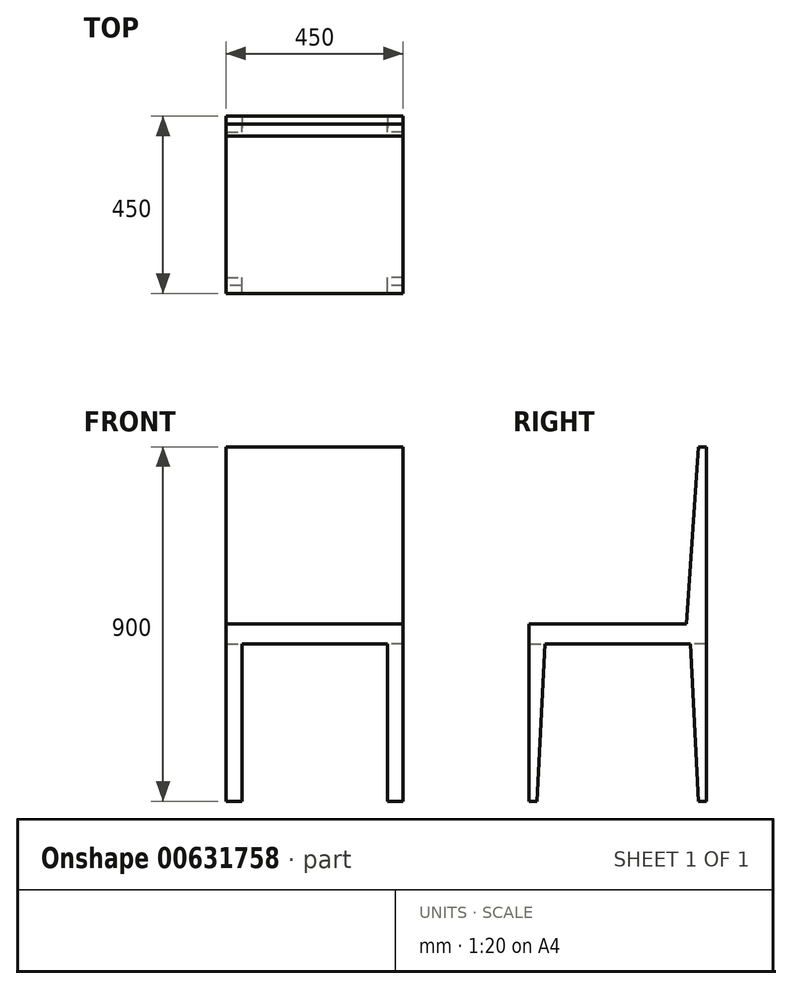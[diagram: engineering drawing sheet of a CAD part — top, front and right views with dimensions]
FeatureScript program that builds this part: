
annotation { "Feature Type Name" : "Feature", "Feature Type Description" : "" }
export const myFeature = defineFeature(function(context is Context, id is Id, definition is map)
    precondition{}
    {
        {
            var Q0;
            Q0=qCreatedBy(makeId("Top.planeOp"),FACE);
            var sketch = newSketch(context, id + "F0", { "sketchPlane" : qUnion([Q0])});
            skLineSegment(sketch, "E0.bottom", {"start": v(0, 0) * mm, "end": v(450, 0) * mm});
            skLineSegment(sketch, "E0.top", {"start": v(0, 450) * mm, "end": v(450, 450) * mm});
            skLineSegment(sketch, "E0.left", {"start": v(0, 0) * mm, "end": v(0, 450) * mm});
            skLineSegment(sketch, "E0.right", {"start": v(450, 0) * mm, "end": v(450, 450) * mm});
            skSolve(sketch);
        }
        {
            var Q0;
            Q0=makeQuery(id+"F0.imprint","IMPRINT",FACE,{"disambiguationData":[TD([[makeQuery(id+"F0.imprint","IMPRINT",EDGE,{"derivedFrom":sQuery(id+"F0.wireOp",EDGE,"E0.bottom")}),1.0]])]});
            extrude(context, id + "F1", {"entities" : qUnion([Q0]), "depth" : 50 * mm, "offsetDistance" : 25 * mm});
        }
        {
            var Q0;
            Q0=makeQuery(id+"F1.opExtrude","CAP_FACE",FACE,{"disambiguationData":[OSD([sQuery(id+"F0.wireOp",EDGE,"E0.bottom"),sQuery(id+"F0.wireOp",EDGE,"E0.top"),sQuery(id+"F0.wireOp",EDGE,"E0.left"),sQuery(id+"F0.wireOp",EDGE,"E0.right")])],"isStart":true});
            var sketch = newSketch(context, id + "F2", { "sketchPlane" : qUnion([Q0])});
            skLineSegment(sketch, "E1.bottom", {"start": v(0, -450) * mm, "end": v(40, -450) * mm});
            skLineSegment(sketch, "E1.top", {"start": v(0, -410) * mm, "end": v(40, -410) * mm});
            skLineSegment(sketch, "E1.left", {"start": v(0, -450) * mm, "end": v(0, -410) * mm});
            skLineSegment(sketch, "E1.right", {"start": v(40, -450) * mm, "end": v(40, -410) * mm});
            skSolve(sketch);
        }
        {
            var Q0;
            Q0=makeQuery(id+"F2.imprint","IMPRINT",FACE,{"disambiguationData":[TD([[makeQuery(id+"F2.imprint","IMPRINT",EDGE,{"derivedFrom":sQuery(id+"F2.wireOp",EDGE,"E1.bottom")}),1.0]])]});
            var Q1;
            Q1=sQuery(id+"F2.wireOp",EDGE,"E1.right");
            extrude(context, id + "F3", {"entities" : qUnion([Q0]), "operationType" : NewBodyOperationType.ADD, "surfaceEntities" : qUnion([Q1]), "depth" : 400 * mm, "offsetDistance" : 25 * mm});
        }
        {
            var Q0;
            Q0=makeQuery(id+"F1.opExtrude","CAP_FACE",FACE,{"disambiguationData":[OSD([sQuery(id+"F0.wireOp",EDGE,"E0.bottom"),sQuery(id+"F0.wireOp",EDGE,"E0.top"),sQuery(id+"F0.wireOp",EDGE,"E0.left"),sQuery(id+"F0.wireOp",EDGE,"E0.right")])],"isStart":true});
            var sketch = newSketch(context, id + "F4", { "sketchPlane" : qUnion([Q0])});
            skLineSegment(sketch, "E2.bottom", {"start": v(0, 0) * mm, "end": v(40, 0) * mm});
            skLineSegment(sketch, "E2.top", {"start": v(0, -40) * mm, "end": v(40, -40) * mm});
            skLineSegment(sketch, "E2.left", {"start": v(0, 0) * mm, "end": v(0, -40) * mm});
            skLineSegment(sketch, "E2.right", {"start": v(40, 0) * mm, "end": v(40, -40) * mm});
            skSolve(sketch);
        }
        {
            var Q0;
            Q0=makeQuery(id+"F4.imprint","IMPRINT",FACE,{"disambiguationData":[TD([[makeQuery(id+"F4.imprint","IMPRINT",EDGE,{"derivedFrom":sQuery(id+"F4.wireOp",EDGE,"E2.bottom")}),-1.0]])]});
            extrude(context, id + "F5", {"entities" : qUnion([Q0]), "operationType" : NewBodyOperationType.ADD, "depth" : 400 * mm, "offsetDistance" : 25 * mm});
        }
        {
            var Q0;
            Q0=makeQuery(id+"F1.opExtrude","CAP_FACE",FACE,{"disambiguationData":[OSD([sQuery(id+"F0.wireOp",EDGE,"E0.bottom"),sQuery(id+"F0.wireOp",EDGE,"E0.top"),sQuery(id+"F0.wireOp",EDGE,"E0.left"),sQuery(id+"F0.wireOp",EDGE,"E0.right")])],"isStart":true});
            var sketch = newSketch(context, id + "F6", { "sketchPlane" : qUnion([Q0])});
            skLineSegment(sketch, "E3.bottom", {"start": v(450, -450) * mm, "end": v(410, -450) * mm});
            skLineSegment(sketch, "E3.top", {"start": v(450, -410) * mm, "end": v(410, -410) * mm});
            skLineSegment(sketch, "E3.left", {"start": v(450, -450) * mm, "end": v(450, -410) * mm});
            skLineSegment(sketch, "E3.right", {"start": v(410, -450) * mm, "end": v(410, -410) * mm});
            skSolve(sketch);
        }
        {
            var Q0;
            Q0 = qSketchRegion(id + "F6", true);
            var Q1;
            Q1=makeQuery(id+"F6.imprint","IMPRINT",FACE,{"disambiguationData":[TD([[makeQuery(id+"F6.imprint","IMPRINT",EDGE,{"derivedFrom":sQuery(id+"F6.wireOp",EDGE,"E3.bottom")}),1.0]])]});
            extrude(context, id + "F7", {"entities" : qUnion([Q0, Q1]), "operationType" : NewBodyOperationType.ADD, "depth" : 400 * mm, "offsetDistance" : 25 * mm});
        }
        {
            var Q0;
            Q0=makeQuery(id+"F1.opExtrude","CAP_FACE",FACE,{"disambiguationData":[OSD([sQuery(id+"F0.wireOp",EDGE,"E0.bottom"),sQuery(id+"F0.wireOp",EDGE,"E0.top"),sQuery(id+"F0.wireOp",EDGE,"E0.left"),sQuery(id+"F0.wireOp",EDGE,"E0.right")])],"isStart":true});
            var sketch = newSketch(context, id + "F8", { "sketchPlane" : qUnion([Q0])});
            skLineSegment(sketch, "E4.bottom", {"start": v(450, 0) * mm, "end": v(410, 0) * mm});
            skLineSegment(sketch, "E4.top", {"start": v(450, -40) * mm, "end": v(410, -40) * mm});
            skLineSegment(sketch, "E4.left", {"start": v(450, 0) * mm, "end": v(450, -40) * mm});
            skLineSegment(sketch, "E4.right", {"start": v(410, 0) * mm, "end": v(410, -40) * mm});
            skSolve(sketch);
        }
        {
            var Q0;
            Q0=makeQuery(id+"F8.imprint","IMPRINT",FACE,{"disambiguationData":[TD([[makeQuery(id+"F8.imprint","IMPRINT",EDGE,{"derivedFrom":sQuery(id+"F8.wireOp",EDGE,"E4.bottom")}),-1.0]])]});
            extrude(context, id + "F9", {"entities" : qUnion([Q0]), "operationType" : NewBodyOperationType.ADD, "depth" : 400 * mm, "offsetDistance" : 25 * mm});
        }
        {
            var Q0;
            Q0=makeQuery(id+"F1.opExtrude","CAP_FACE",FACE,{"disambiguationData":[OSD([sQuery(id+"F0.wireOp",EDGE,"E0.bottom"),sQuery(id+"F0.wireOp",EDGE,"E0.top"),sQuery(id+"F0.wireOp",EDGE,"E0.left"),sQuery(id+"F0.wireOp",EDGE,"E0.right")])],"isStart":false});
            var sketch = newSketch(context, id + "F10", { "sketchPlane" : qUnion([Q0])});
            skLineSegment(sketch, "E5.bottom", {"start": v(450, 450) * mm, "end": v(0, 450) * mm});
            skLineSegment(sketch, "E5.top", {"start": v(450, 400) * mm, "end": v(0, 400) * mm});
            skLineSegment(sketch, "E5.left", {"start": v(450, 450) * mm, "end": v(450, 400) * mm});
            skLineSegment(sketch, "E5.right", {"start": v(0, 450) * mm, "end": v(0, 400) * mm});
            skSolve(sketch);
        }
        {
            var Q0;
            Q0=makeQuery(id+"F10.imprint","IMPRINT",FACE,{"disambiguationData":[TD([[makeQuery(id+"F10.imprint","IMPRINT",EDGE,{"derivedFrom":sQuery(id+"F10.wireOp",EDGE,"E5.bottom")}),-1.0]])]});
            extrude(context, id + "F11", {"entities" : qUnion([Q0]), "operationType" : NewBodyOperationType.ADD, "depth" : 450 * mm, "offsetDistance" : 25 * mm});
        }
        {
            var Q0;
            Q0=makeQuery(id+"F11.boolean.opBoolean","MERGE",FACE,{"derivedFrom":[makeQuery(id+"F9.boolean.opBoolean","MERGE",FACE,{"derivedFrom":[makeQuery(id+"F7.boolean.opBoolean","MERGE",FACE,{"derivedFrom":[makeQuery(id+"F1.opExtrude","SWEPT_FACE",FACE,{"disambiguationData":[OSD([sQuery(id+"F0.wireOp",EDGE,"E0.right")])]}),makeQuery(id+"F7.opExtrude","SWEPT_FACE",FACE,{"disambiguationData":[OSD([sQuery(id+"F6.wireOp",EDGE,"E3.left")])]})]}),makeQuery(id+"F9.opExtrude","SWEPT_FACE",FACE,{"disambiguationData":[OSD([sQuery(id+"F8.wireOp",EDGE,"E4.left")])]})]}),makeQuery(id+"F11.opExtrude","SWEPT_FACE",FACE,{"disambiguationData":[OSD([sQuery(id+"F10.wireOp",EDGE,"E5.left")])]})]});
            var sketch = newSketch(context, id + "F12", { "sketchPlane" : qUnion([Q0])});
            skLineSegment(sketch, "E6", {"start": v(400, 50) * mm, "end": v(430, 500) * mm});
            skLineSegment(sketch, "E7", {"start": v(430, 500) * mm, "end": v(400, 500) * mm});
            skLineSegment(sketch, "E8", {"start": v(400, 500) * mm, "end": v(400, 50) * mm});
            skSolve(sketch);
        }
        {
            var Q0;
            Q0=makeQuery(id+"F12.imprint","IMPRINT",FACE,{"disambiguationData":[TD([[makeQuery(id+"F12.imprint","IMPRINT",EDGE,{"derivedFrom":sQuery(id+"F12.wireOp",EDGE,"E6")}),1.0]])]});
            extrude(context, id + "F13", {"entities" : qUnion([Q0]), "operationType" : NewBodyOperationType.REMOVE, "oppositeDirection" : true, "depth" : 450 * mm, "offsetDistance" : 25 * mm});
        }
        {
            var Q0;
            Q0=makeQuery(id+"F11.boolean.opBoolean","MERGE",FACE,{"derivedFrom":[makeQuery(id+"F5.boolean.opBoolean","MERGE",FACE,{"derivedFrom":[makeQuery(id+"F3.boolean.opBoolean","MERGE",FACE,{"derivedFrom":[makeQuery(id+"F1.opExtrude","SWEPT_FACE",FACE,{"disambiguationData":[OSD([sQuery(id+"F0.wireOp",EDGE,"E0.left")])]}),makeQuery(id+"F3.opExtrude","SWEPT_FACE",FACE,{"disambiguationData":[OSD([sQuery(id+"F2.wireOp",EDGE,"E1.left")])]})]}),makeQuery(id+"F5.opExtrude","SWEPT_FACE",FACE,{"disambiguationData":[OSD([sQuery(id+"F4.wireOp",EDGE,"E2.left")])]})]}),makeQuery(id+"F11.opExtrude","SWEPT_FACE",FACE,{"disambiguationData":[OSD([sQuery(id+"F10.wireOp",EDGE,"E5.right")])]})]});
            var sketch = newSketch(context, id + "F14", { "sketchPlane" : qUnion([Q0])});
            skLineSegment(sketch, "E9", {"start": v(-410, 0) * mm, "end": v(-430, -400) * mm});
            skLineSegment(sketch, "E10", {"start": v(-430, -400) * mm, "end": v(-410, -400) * mm});
            skLineSegment(sketch, "E11", {"start": v(-410, -400) * mm, "end": v(-410, 0) * mm});
            skSolve(sketch);
        }
        {
            var Q0;
            Q0=makeQuery(id+"F14.imprint","IMPRINT",FACE,{"disambiguationData":[TD([[makeQuery(id+"F14.imprint","IMPRINT",EDGE,{"derivedFrom":sQuery(id+"F14.wireOp",EDGE,"E9")}),1.0]])]});
            extrude(context, id + "F15", {"entities" : qUnion([Q0]), "operationType" : NewBodyOperationType.REMOVE, "endBound" : BoundingType.THROUGH_ALL, "oppositeDirection" : true, "depth" : 25 * mm, "offsetDistance" : 25 * mm});
        }
        {
            var Q0;
            Q0=makeQuery(id+"F11.boolean.opBoolean","MERGE",FACE,{"derivedFrom":[makeQuery(id+"F5.boolean.opBoolean","MERGE",FACE,{"derivedFrom":[makeQuery(id+"F3.boolean.opBoolean","MERGE",FACE,{"derivedFrom":[makeQuery(id+"F1.opExtrude","SWEPT_FACE",FACE,{"disambiguationData":[OSD([sQuery(id+"F0.wireOp",EDGE,"E0.left")])]}),makeQuery(id+"F3.opExtrude","SWEPT_FACE",FACE,{"disambiguationData":[OSD([sQuery(id+"F2.wireOp",EDGE,"E1.left")])]})]}),makeQuery(id+"F5.opExtrude","SWEPT_FACE",FACE,{"disambiguationData":[OSD([sQuery(id+"F4.wireOp",EDGE,"E2.left")])]})]}),makeQuery(id+"F11.opExtrude","SWEPT_FACE",FACE,{"disambiguationData":[OSD([sQuery(id+"F10.wireOp",EDGE,"E5.right")])]})]});
            var sketch = newSketch(context, id + "F16", { "sketchPlane" : qUnion([Q0])});
            skLineSegment(sketch, "E12", {"start": v(-40, 0) * mm, "end": v(-20, -400) * mm});
            skLineSegment(sketch, "E13", {"start": v(-20, -400) * mm, "end": v(-40, -400) * mm});
            skLineSegment(sketch, "E14", {"start": v(-40, -400) * mm, "end": v(-40, 0) * mm});
            skSolve(sketch);
        }
        {
            var Q0;
            Q0=makeQuery(id+"F16.imprint","IMPRINT",FACE,{"disambiguationData":[TD([[makeQuery(id+"F16.imprint","IMPRINT",EDGE,{"derivedFrom":sQuery(id+"F16.wireOp",EDGE,"E12")}),-1.0]])]});
            extrude(context, id + "F17", {"entities" : qUnion([Q0]), "operationType" : NewBodyOperationType.REMOVE, "endBound" : BoundingType.THROUGH_ALL, "oppositeDirection" : true, "depth" : 25 * mm, "offsetDistance" : 25 * mm});
        }
        {
            var Q0;
            Q0=makeQuery(id+"F1.opExtrude","CAP_FACE",FACE,{"disambiguationData":[OSD([sQuery(id+"F0.wireOp",EDGE,"E0.bottom"),sQuery(id+"F0.wireOp",EDGE,"E0.top"),sQuery(id+"F0.wireOp",EDGE,"E0.left"),sQuery(id+"F0.wireOp",EDGE,"E0.right")])],"isStart":false});
            extrude(context, id + "F18", {"entities" : qUnion([Q0]), "operationType" : NewBodyOperationType.ADD, "depth" : 100 * mm, "offsetDistance" : 25 * mm});
        }
        {
            var Q0;
            Q0=makeQuery(id+"F18.opExtrude","CAP_FACE",FACE,{"disambiguationData":[OSD([sQuery(id+"F0.wireOp",EDGE,"E0.bottom"),sQuery(id+"F0.wireOp",EDGE,"E0.top"),sQuery(id+"F0.wireOp",EDGE,"E0.left"),sQuery(id+"F0.wireOp",EDGE,"E0.right")])],"isStart":false});
            extrude(context, id + "F19", {"entities" : qUnion([Q0]), "operationType" : NewBodyOperationType.REMOVE, "oppositeDirection" : true, "depth" : 100 * mm, "offsetDistance" : 25 * mm});
        }
    });
